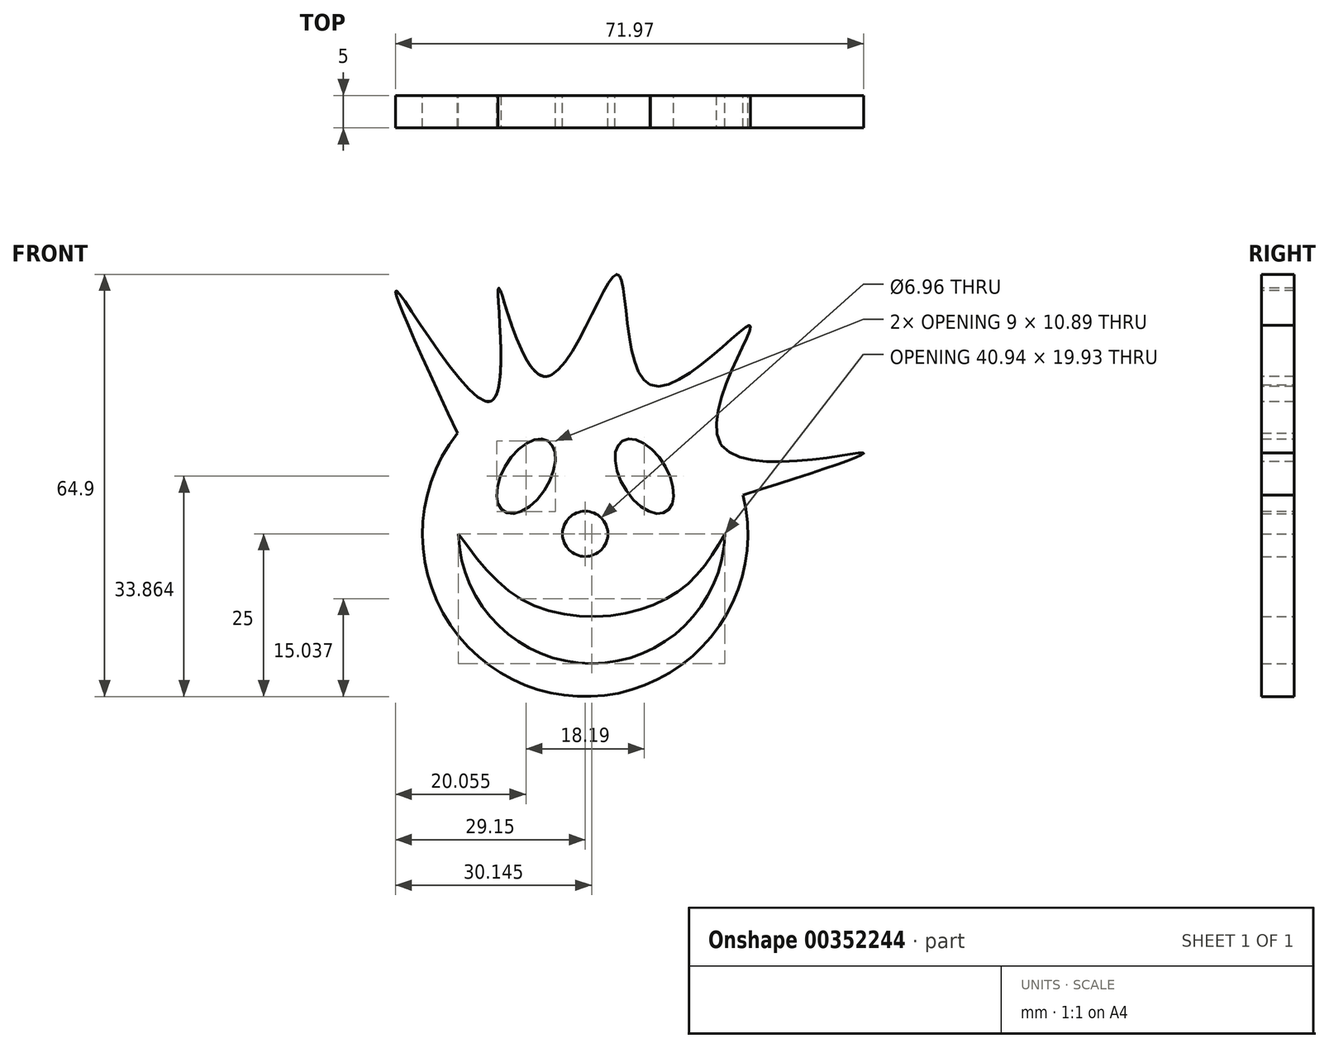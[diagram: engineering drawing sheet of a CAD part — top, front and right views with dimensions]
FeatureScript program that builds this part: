
annotation { "Feature Type Name" : "Feature", "Feature Type Description" : "" }
export const myFeature = defineFeature(function(context is Context, id is Id, definition is map)
    precondition{}
    {
        {
            var Q0;
            Q0=qCreatedBy(makeId("Front.planeOp"),FACE);
            var sketch = newSketch(context, id + "F0", { "sketchPlane" : qUnion([Q0])});
            skArc(sketch, "E0", {"start": v(-19.63, 15.48) * mm, "mid": v(-5.3, -24.43) * mm, "end": v(24.28, 5.97) * mm});
            skEllipse(sketch, "E1", {"center": v(9.1, 8.86) * mm, "majorRadius": 6.4 * mm, "minorRadius": 3.54 * mm, "majorAxis": v(-0.52, 0.85)});
            skEllipse(sketch, "E2.MirrorC", {"center": v(-9.1, 8.86) * mm, "majorRadius": 6.4 * mm, "minorRadius": 3.54 * mm, "majorAxis": v(0.52, 0.85)});
            skArc(sketch, "E3", {"start": v(-19.48, 0) * mm, "mid": v(1, -19.93) * mm, "end": v(21.47, 0) * mm});
            skFitSpline(sketch, "E4", {"points": [v(-19.48, 0) * mm, v(-9.63, -10.16) * mm, v(4.6, -12.46) * mm, v(15.7, -7.75) * mm, v(21.47, 0) * mm], "startDerivative": vector(32.51, -44.35) * mm, "endDerivative": vector(22.17, 38.02) * mm});
            skCircle(sketch, "E5", {"center": v(0, 0) * mm, "radius": 3.48 * mm});
            skFitSpline(sketch, "E6", {"points": [v(-19.63, 15.48) * mm, v(-28.7, 37.07) * mm, v(-14.36, 20.47) * mm, v(-13.3, 37.8) * mm, v(-6.26, 24.2) * mm, v(4.92, 39.9) * mm, v(10.04, 22.9) * mm, v(25.34, 32.04) * mm, v(20.75, 13.94) * mm, v(42.52, 12.46) * mm, v(24.28, 5.97) * mm], "startDerivative": vector(-151.91, 326.99) * mm, "endDerivative": vector(-305.53, -97.9) * mm});
            skArc(sketch, "E7.trimOffspring", {"start": v(-14.2, 20.57) * mm, "mid": v(-14.28, 20.52) * mm, "end": v(-14.36, 20.47) * mm});
            skArc(sketch, "E8.trimOffspring", {"start": v(-5.17, 24.46) * mm, "mid": v(-5.72, 24.34) * mm, "end": v(-6.26, 24.2) * mm});
            skArc(sketch, "E9.trimOffspring", {"start": v(10.04, 22.9) * mm, "mid": v(10, 22.9) * mm, "end": v(9.98, 22.92) * mm});
            skArc(sketch, "E10.trimOffspring", {"start": v(20.98, 13.6) * mm, "mid": v(20.86, 13.77) * mm, "end": v(20.75, 13.94) * mm});
            skCircle(sketch, "E11", {"center": v(-37.9, 8.21) * mm, "radius": 9.78 * mm});
            skSolve(sketch);
        }
        {
            var Q0;
            Q0=makeQuery(id+"F0.imprint","IMPRINT",FACE,{"disambiguationData":[TD([[makeQuery(id+"F0.imprint","IMPRINT",EDGE,{"derivedFrom":sQuery(id+"F0.wireOp",EDGE,"E0")}),1.0]])]});
            extrude(context, id + "F1", {"entities" : qUnion([Q0]), "depth" : 5 * mm});
        }
    });
